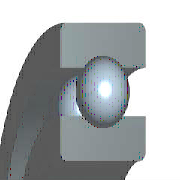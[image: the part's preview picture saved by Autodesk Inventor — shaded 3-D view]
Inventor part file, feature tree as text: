
AUTODESK INVENTOR PART (.ipt)
format: ipt  version: 2023.1 (Build 271208000, 208)  size: 271,360 bytes
history: native  units: mm (DEFAULTED — no unit token found)
features: sketch x1, other x1, pattern_circular x1
ambient origin geometry x8: Origin, YZ Plane, XZ Plane, XY Plane, X Axis, Y Axis, Z Axis, Center Point
bodies: Solid1 (feature_tree), Body (feature_tree)
feature tree (3):
  sketch  "Sketch"  dims[d0=6.5mm d6=90.0deg d7=90.0deg d1=1.0mm d2=100.0mm d3=360.0deg d4=0.0mm d5=0.0mm d8=0.0mm d9=30.0mm d11=55.0mm d12=13.0mm d13=38.15mm d14=0.0mm d15=0.0mm]
  other  "Ball"
  pattern_circular  "Balls"  Angle=90.0deg  [1 undecoded]
note: 1 required parameter value undecoded (feature->parameter linkage not recoverable at this tier; creation-order binding heuristic only, values carry confidence <= 0.55)
